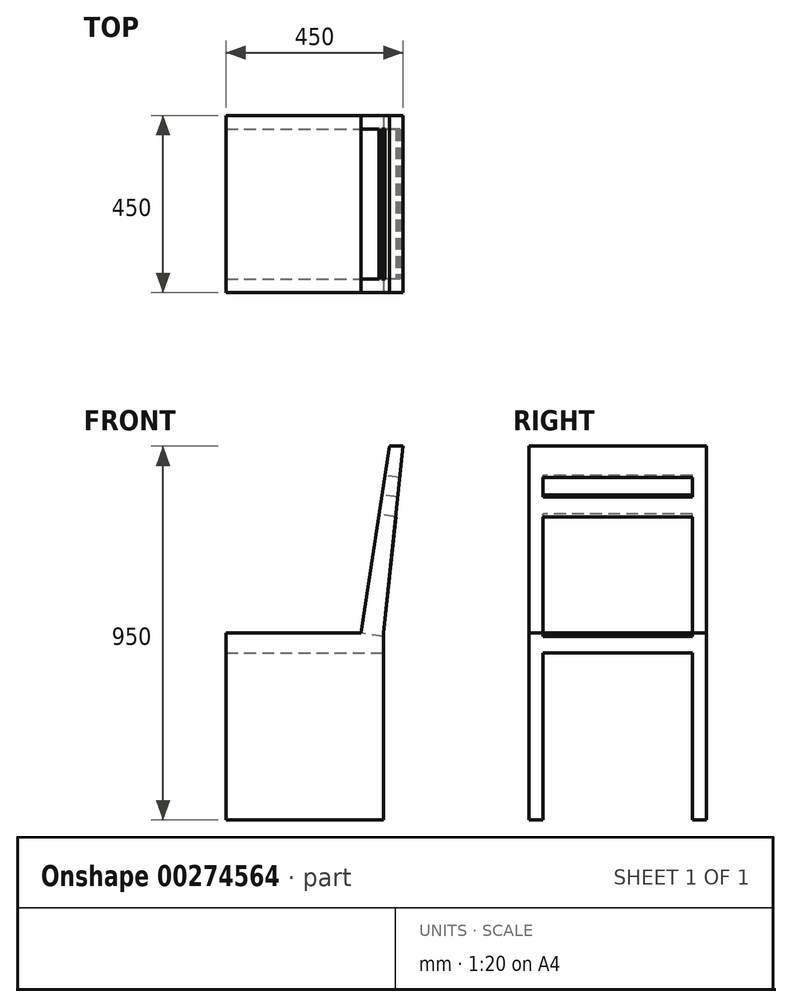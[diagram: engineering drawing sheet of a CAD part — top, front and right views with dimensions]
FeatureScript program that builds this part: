
annotation { "Feature Type Name" : "Feature", "Feature Type Description" : "" }
export const myFeature = defineFeature(function(context is Context, id is Id, definition is map)
    precondition{}
    {
        {
            var Q0;
            Q0=qCreatedBy(makeId("Top.planeOp"),FACE);
            var sketch = newSketch(context, id + "F0", { "sketchPlane" : qUnion([Q0])});
            skLineSegment(sketch, "E0.bottom", {"start": v(225, 225) * mm, "end": v(-225, 225) * mm});
            skLineSegment(sketch, "E0.top", {"start": v(225, -225) * mm, "end": v(-225, -225) * mm});
            skLineSegment(sketch, "E0.left", {"start": v(225, 225) * mm, "end": v(225, -225) * mm});
            skLineSegment(sketch, "E0.right", {"start": v(-225, 225) * mm, "end": v(-225, -225) * mm});
            skPoint(sketch, "E0.middle", {"position": v(0, 0) * mm});
            skSolve(sketch);
        }
        {
            var Q0;
            Q0=qSketchRegion(id+"F0",true);
            extrude(context, id + "F1", {"entities" : qUnion([Q0]), "depth" : 950 * mm});
        }
        {
            var Q0;
            Q0=makeQuery(id+"F1.opExtrude","SWEPT_FACE",FACE,{"disambiguationData":[OSD([sQuery(id+"F0.wireOp",EDGE,"E0.top")])]});
            var sketch = newSketch(context, id + "F2", { "sketchPlane" : qUnion([Q0])});
            skLineSegment(sketch, "E1.bottom", {"start": v(225, 475) * mm, "end": v(-225, 475) * mm});
            skLineSegment(sketch, "E1.top", {"start": v(225, 416.92) * mm, "end": v(-225, 416.92) * mm});
            skLineSegment(sketch, "E1.left", {"start": v(225, 475) * mm, "end": v(225, 416.92) * mm});
            skLineSegment(sketch, "E1.right", {"start": v(-225, 475) * mm, "end": v(-225, 416.92) * mm});
            skLineSegment(sketch, "E2", {"start": v(225, 950) * mm, "end": v(175, 475) * mm});
            skLineSegment(sketch, "E3", {"start": v(190, 950) * mm, "end": v(117.62, 475) * mm});
            skLineSegment(sketch, "E4", {"start": v(117.62, 475) * mm, "end": v(117.62, 0) * mm});
            skLineSegment(sketch, "E5", {"start": v(175, 475) * mm, "end": v(175, 0) * mm});
            skLineSegment(sketch, "E6.bottom", {"start": v(-225, 0) * mm, "end": v(-184.28, 0) * mm});
            skLineSegment(sketch, "E6.top", {"start": v(-225, 0) * mm, "end": v(-184.28, 0) * mm});
            skLineSegment(sketch, "E6.left", {"start": v(-225, 0) * mm, "end": v(-225, 0) * mm});
            skLineSegment(sketch, "E6.right", {"start": v(-184.28, 0) * mm, "end": v(-184.28, 0) * mm});
            skLineSegment(sketch, "E7.top", {"start": v(-184.28, 416.92) * mm, "end": v(-184.28, 416.92) * mm});
            skLineSegment(sketch, "E7.left", {"start": v(-184.28, 0) * mm, "end": v(-184.28, 416.92) * mm});
            skLineSegment(sketch, "E7.right", {"start": v(-184.28, 0) * mm, "end": v(-184.28, 416.92) * mm});
            skSolve(sketch);
        }
        {
            var Q0;
            {var subQ0=sQuery(id+"F2.wireOp",EDGE,"E1.left");Q0=makeQuery(id+"F2.imprint","IMPRINT",FACE,{"disambiguationData":[TD([[makeQuery(id+"F2.imprint","IMPRINT",EDGE,{"derivedFrom":subQ0}),-1.0]])]});}
            var Q1;
            {var subQ4=sQuery(id+"F2.wireOp",EDGE,"E3");Q1=makeQuery(id+"F2.imprint","IMPRINT",FACE,{"disambiguationData":[TD([[makeQuery(id+"F2.imprint","IMPRINT",EDGE,{"derivedFrom":subQ4}),-1.0]])]});}
            var Q2;
            {var subQ4=sQuery(id+"F2.wireOp",EDGE,"E2");Q2=makeQuery(id+"F2.imprint","IMPRINT",FACE,{"disambiguationData":[TD([[makeQuery(id+"F2.imprint","IMPRINT",EDGE,{"derivedFrom":subQ4}),1.0]])]});}
            var Q3;
            {var subQ1=sQuery(id+"F0.wireOp",EDGE,"E0.top");var subQ4=sQuery(id+"F2.wireOp",EDGE,"E5");var subQ6=makeQuery(id+"F1.opExtrude","CAP_EDGE",EDGE,{"disambiguationData":[OSD([subQ1])],"isStart":true});var subQ7=makeQuery(id+"F2.imprint","INTERSECT",VERTEX,{"derivedFrom":[subQ6,subQ4]});Q3=makeQuery(id+"F2.imprint","IMPRINT",FACE,{"disambiguationData":[TD([[makeQuery(id+"F2.imprint","IMPRINT",EDGE,{"disambiguationData":[TD([[subQ7,1.0]])],"derivedFrom":subQ4}),1.0]])]});}
            var Q4;
            {var subQ0=sQuery(id+"F2.wireOp",EDGE,"E7.right");Q4=makeQuery(id+"F2.imprint","IMPRINT",FACE,{"disambiguationData":[TD([[makeQuery(id+"F2.imprint","IMPRINT",EDGE,{"derivedFrom":subQ0}),-1.0]])]});}
            extrude(context, id + "F3", {"entities" : qUnion([Q0, Q1, Q2, Q3, Q4]), "operationType" : NewBodyOperationType.REMOVE, "endBound" : BoundingType.THROUGH_ALL, "oppositeDirection" : true, "depth" : 25 * mm});
        }
        {
            var Q0;
            Q0=makeQuery(id+"F3.boolean.opBoolean","COPY",FACE,{"derivedFrom":makeQuery(id+"F3.opExtrude","SWEPT_FACE",FACE,{"disambiguationData":[OSD([sQuery(id+"F2.wireOp",EDGE,"E5")])]})});
            var sketch = newSketch(context, id + "F4", { "sketchPlane" : qUnion([Q0])});
            skLineSegment(sketch, "E8", {"start": v(-190, 0) * mm, "end": v(-190, 425) * mm});
            skLineSegment(sketch, "E9", {"start": v(-190, 425) * mm, "end": v(190, 425) * mm});
            skLineSegment(sketch, "E10", {"start": v(190, 425) * mm, "end": v(190, 0) * mm});
            skSolve(sketch);
        }
        {
            var Q0;
            Q0 = qSketchRegion(id + "F4", true);
            var Q1;
            {var subQ0=sQuery(id+"F4.wireOp",EDGE,"E8");Q1=makeQuery(id+"F4.imprint","IMPRINT",FACE,{"disambiguationData":[TD([[makeQuery(id+"F4.imprint","IMPRINT",EDGE,{"derivedFrom":subQ0}),-1.0]])]});}
            extrude(context, id + "F5", {"entities" : qUnion([Q0, Q1]), "operationType" : NewBodyOperationType.REMOVE, "endBound" : BoundingType.THROUGH_ALL, "oppositeDirection" : true, "depth" : 25 * mm});
        }
        {
            var Q0;
            Q0=makeQuery(id+"F3.boolean.opBoolean","COPY",FACE,{"derivedFrom":makeQuery(id+"F3.opExtrude","SWEPT_FACE",FACE,{"disambiguationData":[OSD([sQuery(id+"F2.wireOp",EDGE,"E3")])]})});
            var sketch = newSketch(context, id + "F6", { "sketchPlane" : qUnion([Q0])});
            skLineSegment(sketch, "E11", {"start": v(-190, 487.3) * mm, "end": v(-190, 892.78) * mm});
            skLineSegment(sketch, "E12", {"start": v(-190, 892.78) * mm, "end": v(190, 892.78) * mm});
            skLineSegment(sketch, "E13", {"start": v(190, 892.78) * mm, "end": v(190, 487.3) * mm});
            skLineSegment(sketch, "E14", {"start": v(-190, 842.78) * mm, "end": v(190, 842.78) * mm});
            skLineSegment(sketch, "E15", {"start": v(-190, 792.78) * mm, "end": v(190, 792.78) * mm});
            skSolve(sketch);
        }
        {
            var Q0;
            {var subQ0=sQuery(id+"F6.wireOp",EDGE,"E12");Q0=makeQuery(id+"F6.imprint","IMPRINT",FACE,{"disambiguationData":[TD([[makeQuery(id+"F6.imprint","IMPRINT",EDGE,{"derivedFrom":subQ0}),-1.0]])]});}
            var Q1;
            {var subQ3=sQuery(id+"F6.wireOp",EDGE,"E15");Q1=makeQuery(id+"F6.imprint","IMPRINT",FACE,{"disambiguationData":[TD([[makeQuery(id+"F6.imprint","IMPRINT",EDGE,{"derivedFrom":subQ3}),-1.0]])]});}
            extrude(context, id + "F7", {"entities" : qUnion([Q0, Q1]), "operationType" : NewBodyOperationType.REMOVE, "endBound" : BoundingType.THROUGH_ALL, "oppositeDirection" : true, "depth" : 25 * mm});
        }
    });
